# Revit family: 444e9d3d-ae30-460c-a5c6-e2c1ca46f22b
name_source: partatom
category: Generic Models
revit_build: Autodesk Revit 2014 (Build: 20130308_1515(x64)
units: mm (PartAtom-declared; Revit-internal decimal feet)

## types (8) — shared parameters
Assembly Code = B3020100
Construction Details = http://www.arcat.com
Default Elevation = 4' - 0"
Glazing = Glass_Green
Height = 2' - 6 3/4"
Installation-Fabrication = http://glassflooringsystems.com
Keynote = 09 62 83
Manufacturer = Glass Flooring Systems
Manufacturer Website = http://glassflooringsystems.com
Offset From Roof Level = 0' - 0"
Product Data = http://www.arcat.com
Product Properties = http://glassflooringsystems.com
Revision = R1_12-2016
Sales Information = http://glassflooringsystems.com
Specification = http://www.arcat.com
URL = http://glassflooringsystems.com

## per-type parameters (varying)
| type | Description | Frame Finish | Glz Offset | IRafter | Mid Frame | MidRailArry | MidRailSgl | Open Offset | Panels | Spc | TRafter | Width |
| 3 Panel | SkyFloor GlassFloorSys Recessed-ThermBrk Sgl-2-5 - 3 Panel | White Finish | 0' - 2 1/8" | No | 2 | Yes | No | 0' - 1" | 3 | 2' - 6 1/2" | Yes | 7' - 7 1/2" |
| 2 Panel | SkyFloor GlassFloorSys Recessed-ThermBrk Sgl-2-5 - 2 Panel | White Finish | 0' - 2 1/8" | No | 2 | No | Yes | 0' - 1" | 2 | 2' - 6 1/16" | Yes | 5' - 0 1/8" |
| 1 Panel | SkyFloor GlassFloorSys Recessed-ThermBrk Sgl-2-5 - 1 Panel | White Finish | 0' - 2 1/8" | No | 2 | No | No | 0' - 1" | 1 | 2' - 6 3/4" | No | 2' - 6 3/4" |
| 4 Panel | SkyFloor GlassFloorSys Recessed-ThermBrk Sgl-2-5 - 4 Panel | Black Finish | 0' - 2 1/8" | Yes | 3 | Yes | No | 0' - 0 3/4" | 4 | 2' - 6 15/32" | No | 10' - 1 7/8" |
| 5 Panel | SkyFloor GlassFloorSys Recessed-ThermBrk Sgl-2-5 - 5 Panel | White Finish | 0' - 1 3/8" | Yes | 4 | Yes | No | 0' - 1" | 5 | 2' - 6 7/16" | No | 12' - 8 1/4" |
| 6 Panel | SkyFloor GlassFloorSys Recessed-ThermBrk Sgl-2-5 - 6 Panel | White Finish | 0' - 2 1/8" | Yes | 5 | Yes | No | 0' - 1" | 6 | 2' - 6 7/16" | No | 15' - 2 5/8" |
| 7 Panel | SkyFloor GlassFloorSys Recessed-ThermBrk Sgl-2-5 - 7 Panel | White Finish | 0' - 2 1/8" | Yes | 6 | Yes | No | 0' - 1" | 7 | 2' - 6 7/16" | No | 17' - 9" |
| 8 Panel | SkyFloor GlassFloorSys Recessed-ThermBrk Sgl-2-5 - 8 Panel | White Finish | 0' - 2 1/8" | Yes | 7 | Yes | No | 0' - 0 3/4" | 8 | 2' - 6 7/16" | No | 20' - 3 3/8" |

note: column(s) folded — value = type name in every type: Model

## geometry (parser evidence)
native form markers: Sweep x2
no freeform markers — native parametric forms only
